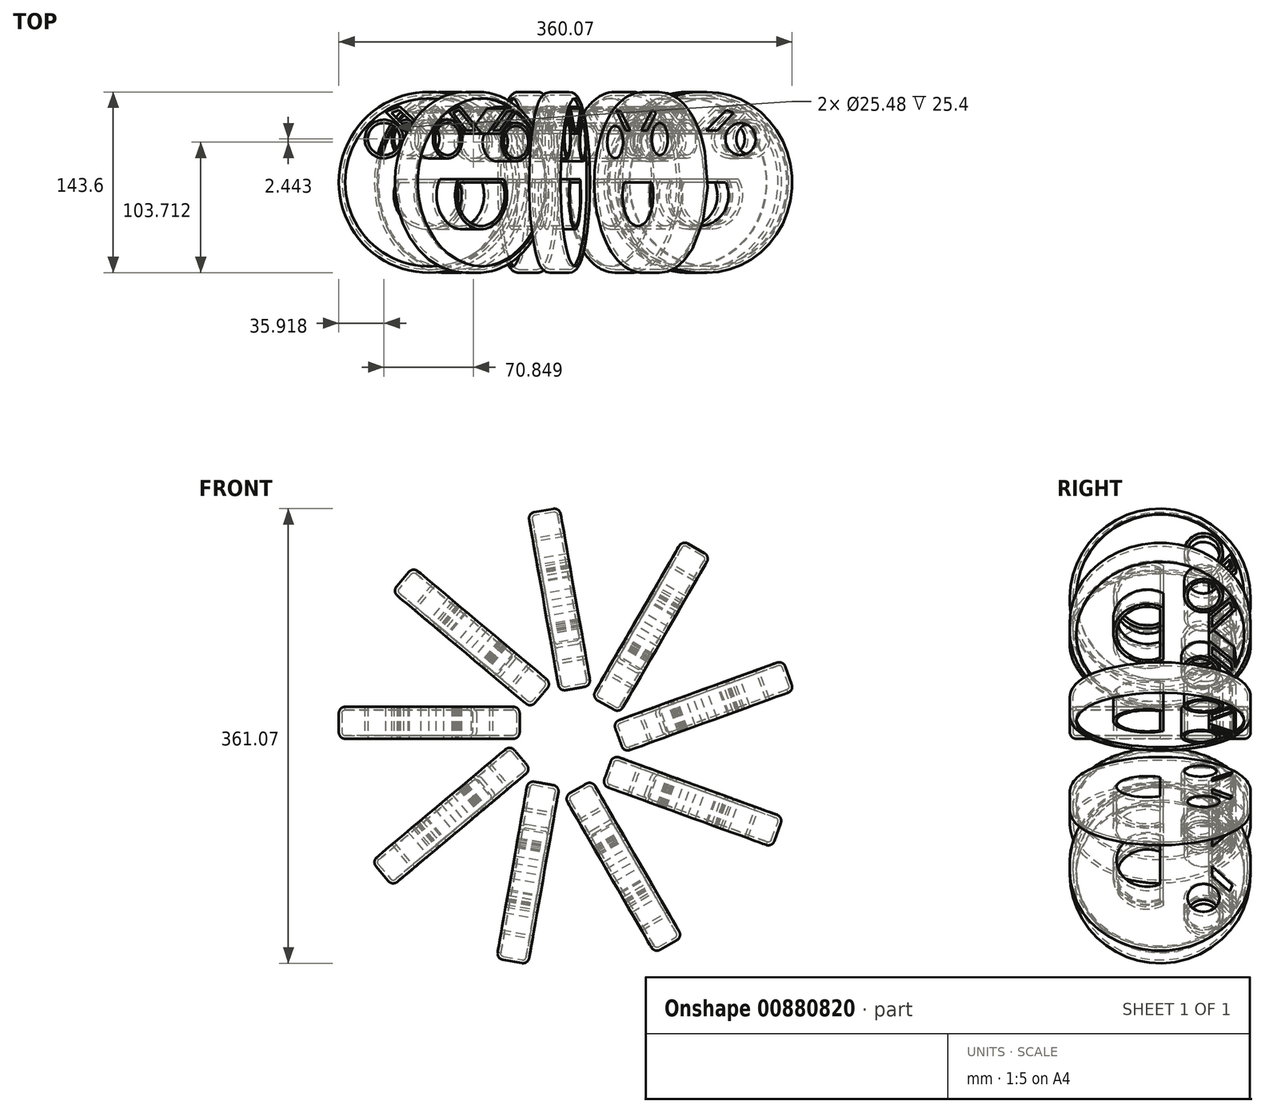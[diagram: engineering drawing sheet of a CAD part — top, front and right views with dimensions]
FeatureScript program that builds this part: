
annotation { "Feature Type Name" : "Feature", "Feature Type Description" : "" }
export const myFeature = defineFeature(function(context is Context, id is Id, definition is map)
    precondition{}
    {
        {
            var Q0;
            Q0=qCreatedBy(makeId("Top.planeOp"),FACE);
            var sketch = newSketch(context, id + "F0", { "sketchPlane" : qUnion([Q0])});
            skCircle(sketch, "E0", {"center": v(0, 0) * mm, "radius": 71.8 * mm});
            skCircle(sketch, "E1", {"center": v(-35.88, 34.36) * mm, "radius": 12.74 * mm});
            skCircle(sketch, "E2", {"center": v(34.97, 31.91) * mm, "radius": 12.74 * mm});
            skArc(sketch, "E3", {"start": v(-23.36, 0) * mm, "mid": v(-1.22, -34.7) * mm, "end": v(20.92, 0) * mm});
            skLineSegment(sketch, "E4", {"start": v(-23.36, 0) * mm, "end": v(20.92, 0) * mm});
            skLineSegment(sketch, "E5", {"start": v(-23.97, 57.26) * mm, "end": v(-6.87, 41.07) * mm});
            skLineSegment(sketch, "E6", {"start": v(-6.87, 41.07) * mm, "end": v(-16.03, 41.07) * mm});
            skLineSegment(sketch, "E7", {"start": v(-16.03, 41.07) * mm, "end": v(-30.08, 55.12) * mm});
            skLineSegment(sketch, "E8", {"start": v(-30.08, 55.12) * mm, "end": v(-23.97, 57.26) * mm});
            skLineSegment(sketch, "E9", {"start": v(17.86, 41.07) * mm, "end": v(33.2, 57.27) * mm});
            skLineSegment(sketch, "E10", {"start": v(33.2, 57.27) * mm, "end": v(25.49, 56.15) * mm});
            skLineSegment(sketch, "E11", {"start": v(25.49, 56.15) * mm, "end": v(11.22, 41.07) * mm});
            skLineSegment(sketch, "E12", {"start": v(11.22, 41.07) * mm, "end": v(17.86, 41.07) * mm});
            skSolve(sketch);
        }
        {
            var Q0;
            Q0=makeQuery(id+"F0.imprint","IMPRINT",FACE,{"disambiguationData":[TD([[makeQuery(id+"F0.imprint","IMPRINT",EDGE,{"derivedFrom":sQuery(id+"F0.wireOp",EDGE,"E0")}),1.0]])]});
            extrude(context, id + "F1", {"entities" : qUnion([Q0]), "depth" : 25.4 * mm, "offsetDistance" : 25.4 * mm});
        }
        {
            var Q0;
            Q0=makeQuery(id+"F1.opExtrude","CAP_EDGE",EDGE,{"disambiguationData":[OSD([sQuery(id+"F0.wireOp",EDGE,"E0")])],"isStart":false});
            var Q1;
            Q1=makeQuery(id+"F1.opExtrude","CAP_EDGE",EDGE,{"disambiguationData":[OSD([sQuery(id+"F0.wireOp",EDGE,"E0")])],"isStart":true});
            fillet(context, id + "F2", {"entities" : qUnion([Q0, Q1]), "radius" : 5.08 * mm, "tangentPropagation" : true, "allowEdgeOverflow" : false});
        }
        {
            var Q0;
            Q0=makeQuery(id+"F1.opExtrude","CAP_FACE",FACE,{"disambiguationData":[OSD([sQuery(id+"F0.wireOp",EDGE,"E0"),sQuery(id+"F0.wireOp",EDGE,"E1"),sQuery(id+"F0.wireOp",EDGE,"E2"),sQuery(id+"F0.wireOp",EDGE,"E3"),sQuery(id+"F0.wireOp",EDGE,"E4"),sQuery(id+"F0.wireOp",EDGE,"E5"),sQuery(id+"F0.wireOp",EDGE,"E6"),sQuery(id+"F0.wireOp",EDGE,"E7"),sQuery(id+"F0.wireOp",EDGE,"E8"),sQuery(id+"F0.wireOp",EDGE,"E9"),sQuery(id+"F0.wireOp",EDGE,"E10"),sQuery(id+"F0.wireOp",EDGE,"E11"),sQuery(id+"F0.wireOp",EDGE,"E12")])],"isStart":false});
            shell(context, id + "F3", {"entities" : qUnion([Q0]), "thickness" : 2.54 * mm});
        }
        {
            var Q0;
            Q0=qCreatedBy(makeId("Top.planeOp"),FACE);
            var sketch = newSketch(context, id + "F4", { "sketchPlane" : qUnion([Q0])});
            skLineSegment(sketch, "E13", {"start": v(110.1, 60) * mm, "end": v(110.1, -64.9) * mm});
            skSolve(sketch);
        }
        {
            var Q0;
            Q0=makeQuery(id+"F1.opExtrude","SWEPT_BODY",BODY,{"disambiguationData":[OSD([sQuery(id+"F0.wireOp",EDGE,"E0"),sQuery(id+"F0.wireOp",EDGE,"E1"),sQuery(id+"F0.wireOp",EDGE,"E2"),sQuery(id+"F0.wireOp",EDGE,"E3"),sQuery(id+"F0.wireOp",EDGE,"E4"),sQuery(id+"F0.wireOp",EDGE,"E5"),sQuery(id+"F0.wireOp",EDGE,"E6"),sQuery(id+"F0.wireOp",EDGE,"E7"),sQuery(id+"F0.wireOp",EDGE,"E8"),sQuery(id+"F0.wireOp",EDGE,"E9"),sQuery(id+"F0.wireOp",EDGE,"E10"),sQuery(id+"F0.wireOp",EDGE,"E11"),sQuery(id+"F0.wireOp",EDGE,"E12")])]});
            var Q1;
            Q1=sQuery(id+"F4.wireOp",EDGE,"E13");
            circularPattern(context, id + "F5", {"entities" : qUnion([Q0]), "axis" : qUnion([Q1]), "angle" : 360 * degree, "instanceCount" : 9, "oppositeDirection" : true, "equalSpace" : true});
        }
    });
